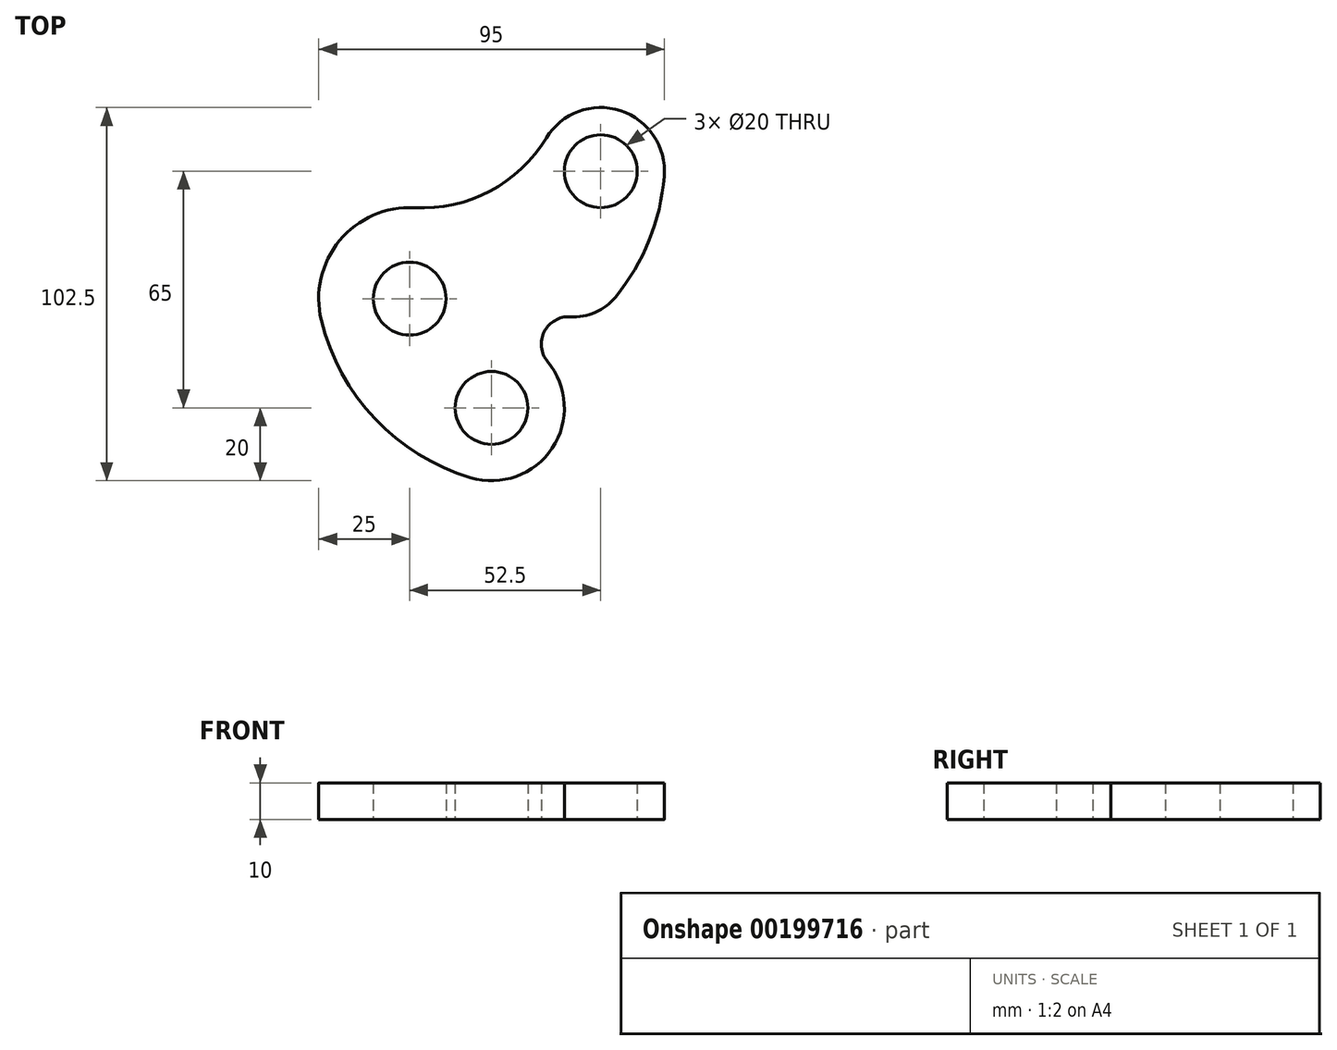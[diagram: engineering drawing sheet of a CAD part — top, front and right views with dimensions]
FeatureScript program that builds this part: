
annotation { "Feature Type Name" : "Feature", "Feature Type Description" : "" }
export const myFeature = defineFeature(function(context is Context, id is Id, definition is map)
    precondition{}
    {
        {
            var Q0;
            Q0=qCreatedBy(makeId("Top.planeOp"),FACE);
            var sketch = newSketch(context, id + "F0", { "sketchPlane" : qUnion([Q0])});
            skCircle(sketch, "E0", {"center": v(0, 0) * mm, "radius": 10 * mm});
            skCircle(sketch, "E1", {"center": v(52.5, 35) * mm, "radius": 10 * mm});
            skCircle(sketch, "E2", {"center": v(22.5, -30) * mm, "radius": 10 * mm});
            skArc(sketch, "E3", {"start": v(37.55, 44.1) * mm, "mid": v(57.9, 51.64) * mm, "end": v(69.94, 33.58) * mm});
            skArc(sketch, "E4", {"start": v(37.9, -17.24) * mm, "mid": v(39.17, -41.05) * mm, "end": v(16.75, -49.16) * mm});
            skArc(sketch, "E5", {"start": v(1.3, 24.97) * mm, "mid": v(-19.26, 15.94) * mm, "end": v(-24.28, -5.94) * mm});
            skArc(sketch, "E6", {"start": v(1.3, 24.97) * mm, "mid": v(22.07, 29.54) * mm, "end": v(37.55, 44.1) * mm});
            skArc(sketch, "E7", {"start": v(-24.28, -5.94) * mm, "mid": v(-9.51, -33) * mm, "end": v(16.75, -49.16) * mm});
            skArc(sketch, "E8", {"start": v(44.12, -4.97) * mm, "mid": v(51.03, -3.73) * mm, "end": v(56.62, 0.51) * mm});
            skArc(sketch, "E9", {"start": v(56.62, 0.51) * mm, "mid": v(65.8, 16.03) * mm, "end": v(69.94, 33.58) * mm});
            skArc(sketch, "E10", {"start": v(44.12, -4.97) * mm, "mid": v(37, -9.07) * mm, "end": v(37.9, -17.24) * mm});
            skSolve(sketch);
        }
        {
            var Q0;
            Q0=makeQuery(id+"F0.imprint","IMPRINT",FACE,{"disambiguationData":[TD([[makeQuery(id+"F0.imprint","IMPRINT",EDGE,{"derivedFrom":sQuery(id+"F0.wireOp",EDGE,"E0")}),-1.0]])]});
            extrude(context, id + "F1", {"entities" : qUnion([Q0]), "depth" : 10 * mm});
        }
    });
